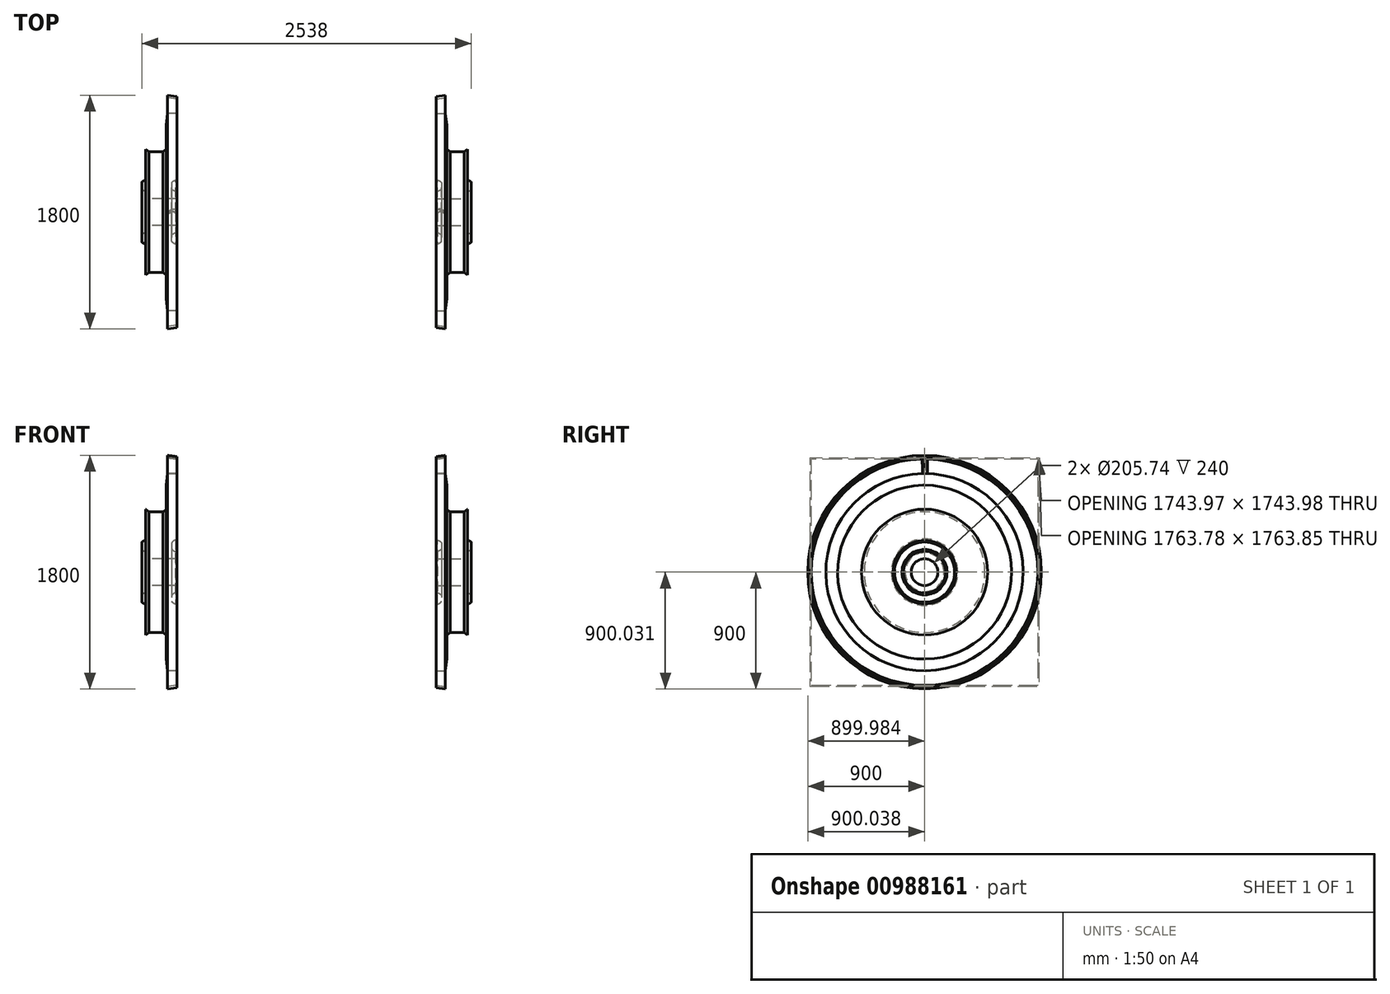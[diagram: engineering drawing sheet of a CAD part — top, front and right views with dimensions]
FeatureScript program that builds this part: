
annotation { "Feature Type Name" : "Feature", "Feature Type Description" : "" }
export const myFeature = defineFeature(function(context is Context, id is Id, definition is map)
    precondition{}
    {
        {
            var Q0;
            Q0=qCreatedBy(makeId("Top.planeOp"),FACE);
            var sketch = newSketch(context, id + "F0", { "sketchPlane" : qUnion([Q0])});
            skLineSegment(sketch, "E0", {"start": v(-458.73, 0) * mm, "end": v(0, 0) * mm, "construction": true});
            skLineSegment(sketch, "E1", {"start": v(0, 760) * mm, "end": v(-70, 760) * mm});
            skLineSegment(sketch, "E2", {"start": v(-105, 465) * mm, "end": v(-215, 465) * mm});
            skLineSegment(sketch, "E3", {"start": v(-215, 465) * mm, "end": v(-240, 485) * mm});
            skLineSegment(sketch, "E4", {"start": v(-240, 485) * mm, "end": v(-240, 243.87) * mm});
            skLineSegment(sketch, "E5", {"start": v(-240, 102.87) * mm, "end": v(0, 102.87) * mm});
            skLineSegment(sketch, "E6", {"start": v(0, 102.87) * mm, "end": v(0, 157.87) * mm});
            skLineSegment(sketch, "E7", {"start": v(-70, 900) * mm, "end": v(-70, 882) * mm});
            skLineSegment(sketch, "E8", {"start": v(-70, 882) * mm, "end": v(0, 872) * mm});
            skLineSegment(sketch, "E9", {"start": v(0, 872) * mm, "end": v(0, 890) * mm});
            skLineSegment(sketch, "E10", {"start": v(0, 890) * mm, "end": v(-70, 900) * mm});
            skLineSegment(sketch, "E11", {"start": v(-70, 760) * mm, "end": v(-70, 882) * mm, "construction": true});
            skLineSegment(sketch, "E12", {"start": v(-80, 485) * mm, "end": v(-80, 670) * mm});
            skLineSegment(sketch, "E13", {"start": v(-80, 670) * mm, "end": v(-70, 760) * mm});
            skLineSegment(sketch, "E14", {"start": v(-80, 485) * mm, "end": v(-105, 465) * mm});
            skLineSegment(sketch, "E15", {"start": v(-80, 485) * mm, "end": v(-240, 485) * mm, "construction": true});
            skArc(sketch, "E16", {"start": v(-240, 161.87) * mm, "mid": v(-255.7, 165) * mm, "end": v(-269, 173.89) * mm});
            skLineSegment(sketch, "E17", {"start": v(-269, 231.85) * mm, "end": v(-269, 173.89) * mm});
            skArc(sketch, "E18.trimOffspring", {"start": v(-269, 231.85) * mm, "mid": v(-255.7, 240.75) * mm, "end": v(-240, 243.87) * mm});
            skLineSegment(sketch, "E19.trimOffspring", {"start": v(-240, 161.87) * mm, "end": v(-240, 102.87) * mm});
            skArc(sketch, "E20", {"start": v(-240, 161.87) * mm, "mid": v(-281, 202.87) * mm, "end": v(-240, 243.87) * mm, "construction": true});
            skLineSegment(sketch, "E21", {"start": v(-240, 202.87) * mm, "end": v(0, 202.87) * mm, "construction": true});
            skArc(sketch, "E22", {"start": v(0, 157.87) * mm, "mid": v(-22.53, 163.91) * mm, "end": v(-39, 180.42) * mm});
            skLineSegment(sketch, "E23", {"start": v(-39, 225.32) * mm, "end": v(-39, 180.42) * mm});
            skArc(sketch, "E24.trimOffspring", {"start": v(-39, 225.32) * mm, "mid": v(-22.53, 241.83) * mm, "end": v(0, 247.87) * mm});
            skLineSegment(sketch, "E25.trimOffspring", {"start": v(0, 247.87) * mm, "end": v(0, 760) * mm});
            skArc(sketch, "E26", {"start": v(0, 157.87) * mm, "mid": v(-45, 202.87) * mm, "end": v(0, 247.87) * mm, "construction": true});
            skSolve(sketch);
        }
        {
            var Q0;
            Q0=makeQuery(id+"F0.imprint","IMPRINT",FACE,{"disambiguationData":[TD([[makeQuery(id+"F0.imprint","IMPRINT",EDGE,{"derivedFrom":sQuery(id+"F0.wireOp",EDGE,"E7")}),1.0]])]});
            var Q1;
            Q1=makeQuery(id+"F0.imprint","IMPRINT",FACE,{"disambiguationData":[TD([[makeQuery(id+"F0.imprint","IMPRINT",EDGE,{"derivedFrom":sQuery(id+"F0.wireOp",EDGE,"E1")}),1.0]])]});
            var Q2;
            Q2=sQuery(id+"F0.wireOp",EDGE,"E0");
            revolve(context, id + "F1", {"surfaceOperationType" : NewSurfaceOperationType.NEW, "entities" : qUnion([Q0, Q1]), "axis" : qUnion([Q2]), "revolveType" : RevolveType.FULL});
        }
        {
            var Q0;
            Q0=makeQuery(id+"F1.opRevolve","SWEPT_EDGE",EDGE,{"disambiguationData":[OSD([sQuery(id+"F0.wireOp",EDGE,"E24.trimOffspring"),sQuery(id+"F0.wireOp",EDGE,"E25.trimOffspring")])]});
            var Q1;
            Q1=makeQuery(id+"F1.opRevolve","SWEPT_EDGE",EDGE,{"disambiguationData":[OSD([sQuery(id+"F0.wireOp",EDGE,"E6"),sQuery(id+"F0.wireOp",EDGE,"E22")])]});
            chamfer(context, id + "F2", {"entities" : qUnion([Q0, Q1]), "width" : 9 * mm, "tangentPropagation" : true});
        }
        {
            var Q0;
            Q0=qCreatedBy(makeId("Right.planeOp"),FACE);
            var sketch = newSketch(context, id + "F3", { "sketchPlane" : qUnion([Q0])});
            skLineSegment(sketch, "E27", {"start": v(0, 0) * mm, "end": v(0, 760) * mm, "construction": true});
            skLineSegment(sketch, "E28", {"start": v(0, 0) * mm, "end": v(0, 890) * mm, "construction": true});
            skCircle(sketch, "E29.0", {"center": v(0, 0) * mm, "radius": 890 * mm, "construction": true});
            skCircle(sketch, "E30.0", {"center": v(0, 0) * mm, "radius": 760 * mm, "construction": true});
            skSolve(sketch);
        }
        {
            var Q0;
            Q0=sQuery(id+"F3.wireOp",VERTEX,"E28.end");
            var Q1;
            Q1=sQuery(id+"F3.wireOp",EDGE,"E28");
            cPlane(context, id + "F4", {"entities" : qUnion([Q0, Q1]), "cplaneType" : CPlaneType.LINE_POINT, "offset" : 25 * mm, "width" : 150 * mm, "height" : 150 * mm});
        }
        {
            var Q0;
            Q0=sQuery(id+"F3.wireOp",VERTEX,"E27.end");
            var Q1;
            Q1=sQuery(id+"F3.wireOp",EDGE,"E28");
            cPlane(context, id + "F5", {"entities" : qUnion([Q0, Q1]), "cplaneType" : CPlaneType.LINE_POINT, "offset" : 25 * mm, "width" : 150 * mm, "height" : 150 * mm});
        }
        {
            var Q0;
            Q0=qCreatedBy(id+"F5.planeOp",FACE);
            cPlane(context, id + "F6", {"entities" : qUnion([Q0]), "cplaneType" : CPlaneType.OFFSET, "offset" : 1 * mm, "oppositeDirection" : true, "width" : 150 * mm, "height" : 150 * mm});
        }
        {
            var Q0;
            Q0=qCreatedBy(id+"F4.planeOp",FACE);
            cPlane(context, id + "F7", {"entities" : qUnion([Q0]), "cplaneType" : CPlaneType.OFFSET, "offset" : 5 * mm, "oppositeDirection" : true, "width" : 150 * mm, "height" : 150 * mm});
        }
        {
            var Q0;
            Q0=qCreatedBy(id+"F6.planeOp",FACE);
            var sketch = newSketch(context, id + "F8", { "sketchPlane" : qUnion([Q0])});
            skLineSegment(sketch, "E31.0", {"start": v(-70, -760) * mm, "end": v(-70, 760) * mm, "construction": true});
            skLineSegment(sketch, "E32.0", {"start": v(0, 760) * mm, "end": v(0, -760) * mm, "construction": true});
            skLineSegment(sketch, "E33", {"start": v(0, 0) * mm, "end": v(0, 15) * mm});
            skLineSegment(sketch, "E34", {"start": v(-70, -5.85) * mm, "end": v(-70, -15.85) * mm});
            skFitSpline(sketch, "E35", {"points": [v(0, 15) * mm, v(-24.64, 24.17) * mm, v(-44.06, 19.52) * mm, v(-70, -5.85) * mm], "startDerivative": vector(-111.88, 66.6) * mm, "endDerivative": vector(-58.12, -78.29) * mm});
            skFitSpline(sketch, "E36", {"points": [v(0, 0) * mm, v(-12.17, -4.37) * mm, v(-24.8, 4.42) * mm, v(-70, -15.85) * mm], "startDerivative": vector(-53.5, -50.52) * mm, "endDerivative": vector(-90.02, -90.02) * mm});
            skLineSegment(sketch, "E37", {"start": v(-70, -15.85) * mm, "end": v(-55.5, -1.34) * mm, "construction": true});
            skLineSegment(sketch, "E38", {"start": v(-70, -15.85) * mm, "end": v(-53.35, -15.85) * mm, "construction": true});
            skSolve(sketch);
        }
        {
            var Q0;
            Q0=qCreatedBy(id+"F7.planeOp",FACE);
            var sketch = newSketch(context, id + "F9", { "sketchPlane" : qUnion([Q0])});
            skLineSegment(sketch, "E39.0", {"start": v(0, 890) * mm, "end": v(0, -890) * mm, "construction": true});
            skLineSegment(sketch, "E40.0", {"start": v(-70, -900) * mm, "end": v(-70, 900) * mm, "construction": true});
            skLineSegment(sketch, "E41", {"start": v(-70, -8.63) * mm, "end": v(-70, -18.63) * mm});
            skLineSegment(sketch, "E42", {"start": v(0, 10.79) * mm, "end": v(0, -4.21) * mm});
            skFitSpline(sketch, "E43", {"points": [v(0, 10.79) * mm, v(-21.81, 20.85) * mm, v(-44.22, 16.04) * mm, v(-70, -8.63) * mm], "startDerivative": vector(-60.38, 73.82) * mm, "endDerivative": vector(-79.96, -117.81) * mm});
            skFitSpline(sketch, "E44", {"points": [v(0, -4.21) * mm, v(-13.51, -5.54) * mm, v(-26.13, 3.59) * mm, v(-70, -18.63) * mm], "startDerivative": vector(-80.99, -68.84) * mm, "endDerivative": vector(-100.38, -91.74) * mm});
            skSolve(sketch);
        }
        {
            var Q2;
            Q2=qSketchRegion(id+"F8",true);
            var Q3;
            Q3=qSketchRegion(id+"F9",true);
            loft(context, id + "F10", {"operationType" : NewBodyOperationType.ADD, "sheetProfilesArray" : [{ "sheetProfileEntities" : qUnion([Q2]) }, { "sheetProfileEntities" : qUnion([Q3]) }]});
        }
        {
            var Q0;
            Q0=qCreatedBy(makeId("Right.planeOp"),FACE);
            cPlane(context, id + "F11", {"entities" : qUnion([Q0]), "cplaneType" : CPlaneType.OFFSET, "offset" : 1000 * mm, "width" : 150 * mm, "height" : 150 * mm});
        }
        {
            var Q0;
            Q0=makeQuery(id+"F1.opRevolve","SWEPT_BODY",BODY,{"disambiguationData":[OSD([sQuery(id+"F0.wireOp",EDGE,"E1"),sQuery(id+"F0.wireOp",EDGE,"E2"),sQuery(id+"F0.wireOp",EDGE,"E3"),sQuery(id+"F0.wireOp",EDGE,"E4"),sQuery(id+"F0.wireOp",EDGE,"E5"),sQuery(id+"F0.wireOp",EDGE,"E6"),sQuery(id+"F0.wireOp",EDGE,"E12"),sQuery(id+"F0.wireOp",EDGE,"E13"),sQuery(id+"F0.wireOp",EDGE,"E14"),sQuery(id+"F0.wireOp",EDGE,"E16"),sQuery(id+"F0.wireOp",EDGE,"E17"),sQuery(id+"F0.wireOp",EDGE,"E18.trimOffspring"),sQuery(id+"F0.wireOp",EDGE,"E19.trimOffspring"),sQuery(id+"F0.wireOp",EDGE,"E22"),sQuery(id+"F0.wireOp",EDGE,"E23"),sQuery(id+"F0.wireOp",EDGE,"E24.trimOffspring"),sQuery(id+"F0.wireOp",EDGE,"E25.trimOffspring")])]});
            var Q1;
            Q1=qCreatedBy(id+"F11.planeOp",FACE);
            mirror(context, id + "F12", {"entities" : qUnion([Q0]), "mirrorPlane" : qUnion([Q1])});
        }
    });
